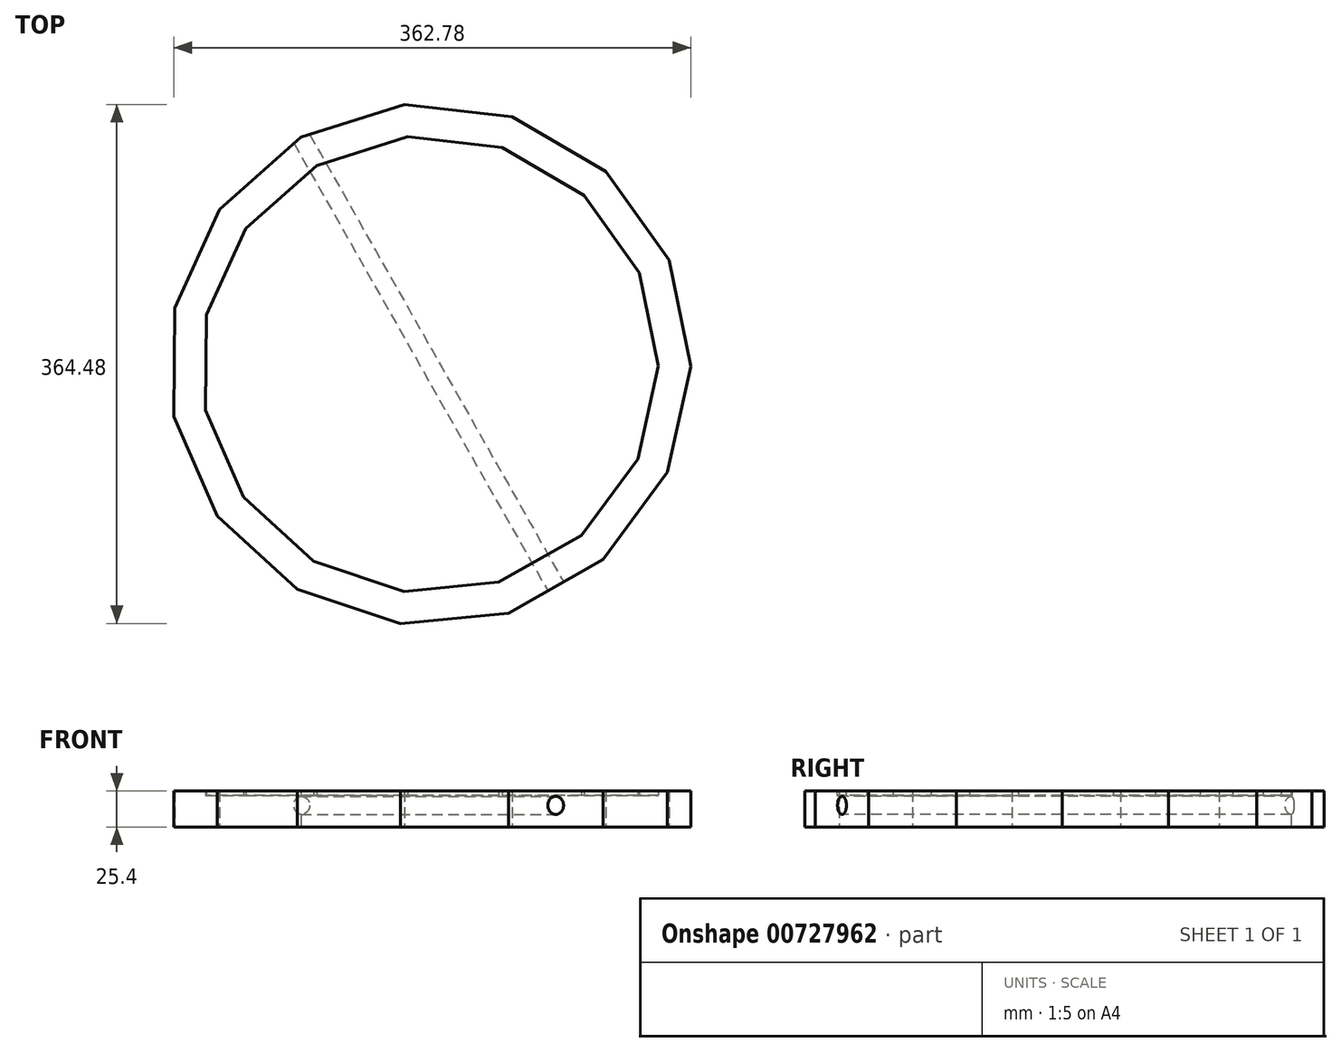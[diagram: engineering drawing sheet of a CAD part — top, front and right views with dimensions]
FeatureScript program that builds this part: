
annotation { "Feature Type Name" : "Feature", "Feature Type Description" : "" }
export const myFeature = defineFeature(function(context is Context, id is Id, definition is map)
    precondition{}
    {
        {
            var Q0;
            Q0=qCreatedBy(makeId("Top.planeOp"),FACE);
            var sketch = newSketch(context, id + "F0", { "sketchPlane" : qUnion([Q0])});
            skCircle(sketch, "E0.cCircle", {"center": v(0, 0) * mm, "radius": 179.25 * mm, "construction": true});
            skLineSegment(sketch, "E0.0", {"start": v(-178.95, 39.48) * mm, "end": v(-147.42, 108.85) * mm});
            skLineSegment(sketch, "E0.1", {"start": v(-147.42, 108.85) * mm, "end": v(-90.4, 159.4) * mm});
            skLineSegment(sketch, "E0.2", {"start": v(-90.4, 159.4) * mm, "end": v(-17.76, 182.39) * mm});
            skLineSegment(sketch, "E0.3", {"start": v(-17.76, 182.39) * mm, "end": v(57.96, 173.84) * mm});
            skLineSegment(sketch, "E0.4", {"start": v(57.96, 173.84) * mm, "end": v(123.66, 135.24) * mm});
            skLineSegment(sketch, "E0.5", {"start": v(123.66, 135.24) * mm, "end": v(167.98, 73.25) * mm});
            skLineSegment(sketch, "E0.6", {"start": v(167.98, 73.25) * mm, "end": v(183.25, -1.4) * mm});
            skLineSegment(sketch, "E0.7", {"start": v(183.25, -1.4) * mm, "end": v(166.83, -75.82) * mm});
            skLineSegment(sketch, "E0.8", {"start": v(166.83, -75.82) * mm, "end": v(121.57, -137.12) * mm});
            skLineSegment(sketch, "E0.9", {"start": v(121.57, -137.12) * mm, "end": v(55.29, -174.71) * mm});
            skLineSegment(sketch, "E0.10", {"start": v(55.29, -174.71) * mm, "end": v(-20.55, -182.1) * mm});
            skLineSegment(sketch, "E0.11", {"start": v(-20.55, -182.1) * mm, "end": v(-92.84, -158) * mm});
            skLineSegment(sketch, "E0.12", {"start": v(-92.84, -158) * mm, "end": v(-149.08, -106.57) * mm});
            skLineSegment(sketch, "E0.13", {"start": v(-149.08, -106.57) * mm, "end": v(-179.53, -36.72) * mm});
            skLineSegment(sketch, "E0.14", {"start": v(-179.53, -36.72) * mm, "end": v(-178.95, 39.48) * mm});
            skPoint(sketch, "E0.0.midPoint", {"position": v(-163.19, 74.16) * mm});
            skSolve(sketch);
        }
        {
            var Q0;
            Q0=makeQuery(id+"F0.imprint","IMPRINT",FACE,{"disambiguationData":[TD([[makeQuery(id+"F0.imprint","IMPRINT",EDGE,{"derivedFrom":sQuery(id+"F0.wireOp",EDGE,"E0.0")}),-1.0]])]});
            extrude(context, id + "F1", {"entities" : qUnion([Q0]), "depth" : 25.4 * mm, "offsetDistance" : 25.4 * mm});
        }
        {
            var Q0;
            Q0=makeQuery(id+"F1.opExtrude","CAP_FACE",FACE,{"disambiguationData":[OSD([sQuery(id+"F0.wireOp",EDGE,"E0.0"),sQuery(id+"F0.wireOp",EDGE,"E0.1"),sQuery(id+"F0.wireOp",EDGE,"E0.2"),sQuery(id+"F0.wireOp",EDGE,"E0.3"),sQuery(id+"F0.wireOp",EDGE,"E0.4"),sQuery(id+"F0.wireOp",EDGE,"E0.5"),sQuery(id+"F0.wireOp",EDGE,"E0.6"),sQuery(id+"F0.wireOp",EDGE,"E0.7"),sQuery(id+"F0.wireOp",EDGE,"E0.8"),sQuery(id+"F0.wireOp",EDGE,"E0.9"),sQuery(id+"F0.wireOp",EDGE,"E0.10"),sQuery(id+"F0.wireOp",EDGE,"E0.11"),sQuery(id+"F0.wireOp",EDGE,"E0.12"),sQuery(id+"F0.wireOp",EDGE,"E0.13"),sQuery(id+"F0.wireOp",EDGE,"E0.14")])],"isStart":false});
            shell(context, id + "F2", {"entities" : qUnion([Q0]), "thickness" : 22.22 * mm});
        }
        {
            var Q0;
            Q0=makeQuery(id+"F1.opExtrude","SWEPT_FACE",FACE,{"disambiguationData":[OSD([sQuery(id+"F0.wireOp",EDGE,"E0.9")])]});
            var sketch = newSketch(context, id + "F3", { "sketchPlane" : qUnion([Q0])});
            skPoint(sketch, "E1", {"position": v(0, 15.25) * mm});
            skPoint(sketch, "E1.positionSnap0", {"position": v(0, 0) * mm});
            skSolve(sketch);
        }
        {
            var Q0;
            Q0=sQuery(id+"F3.wireOp",VERTEX,"E1");
            var Q1;
            Q1=makeQuery(id+"F1.opExtrude","SWEPT_BODY",BODY,{"disambiguationData":[OSD([sQuery(id+"F0.wireOp",EDGE,"E0.0"),sQuery(id+"F0.wireOp",EDGE,"E0.1"),sQuery(id+"F0.wireOp",EDGE,"E0.2"),sQuery(id+"F0.wireOp",EDGE,"E0.3"),sQuery(id+"F0.wireOp",EDGE,"E0.4"),sQuery(id+"F0.wireOp",EDGE,"E0.5"),sQuery(id+"F0.wireOp",EDGE,"E0.6"),sQuery(id+"F0.wireOp",EDGE,"E0.7"),sQuery(id+"F0.wireOp",EDGE,"E0.8"),sQuery(id+"F0.wireOp",EDGE,"E0.9"),sQuery(id+"F0.wireOp",EDGE,"E0.10"),sQuery(id+"F0.wireOp",EDGE,"E0.11"),sQuery(id+"F0.wireOp",EDGE,"E0.12"),sQuery(id+"F0.wireOp",EDGE,"E0.13"),sQuery(id+"F0.wireOp",EDGE,"E0.14")])]});
            hole(context, id + "F4", {"style" : HoleStyle.SIMPLE, "endStyle" : HoleEndStyle.THROUGH, "holeDiameter" : 12.7 * mm, "majorDiameter" : 6.35 * mm, "isTappedThrough" : true, "tappedDepth" : 12.7 * mm, "tapClearance" : 3, "locations" : qUnion([Q0]), "scope" : qUnion([Q1])});
        }
    });
